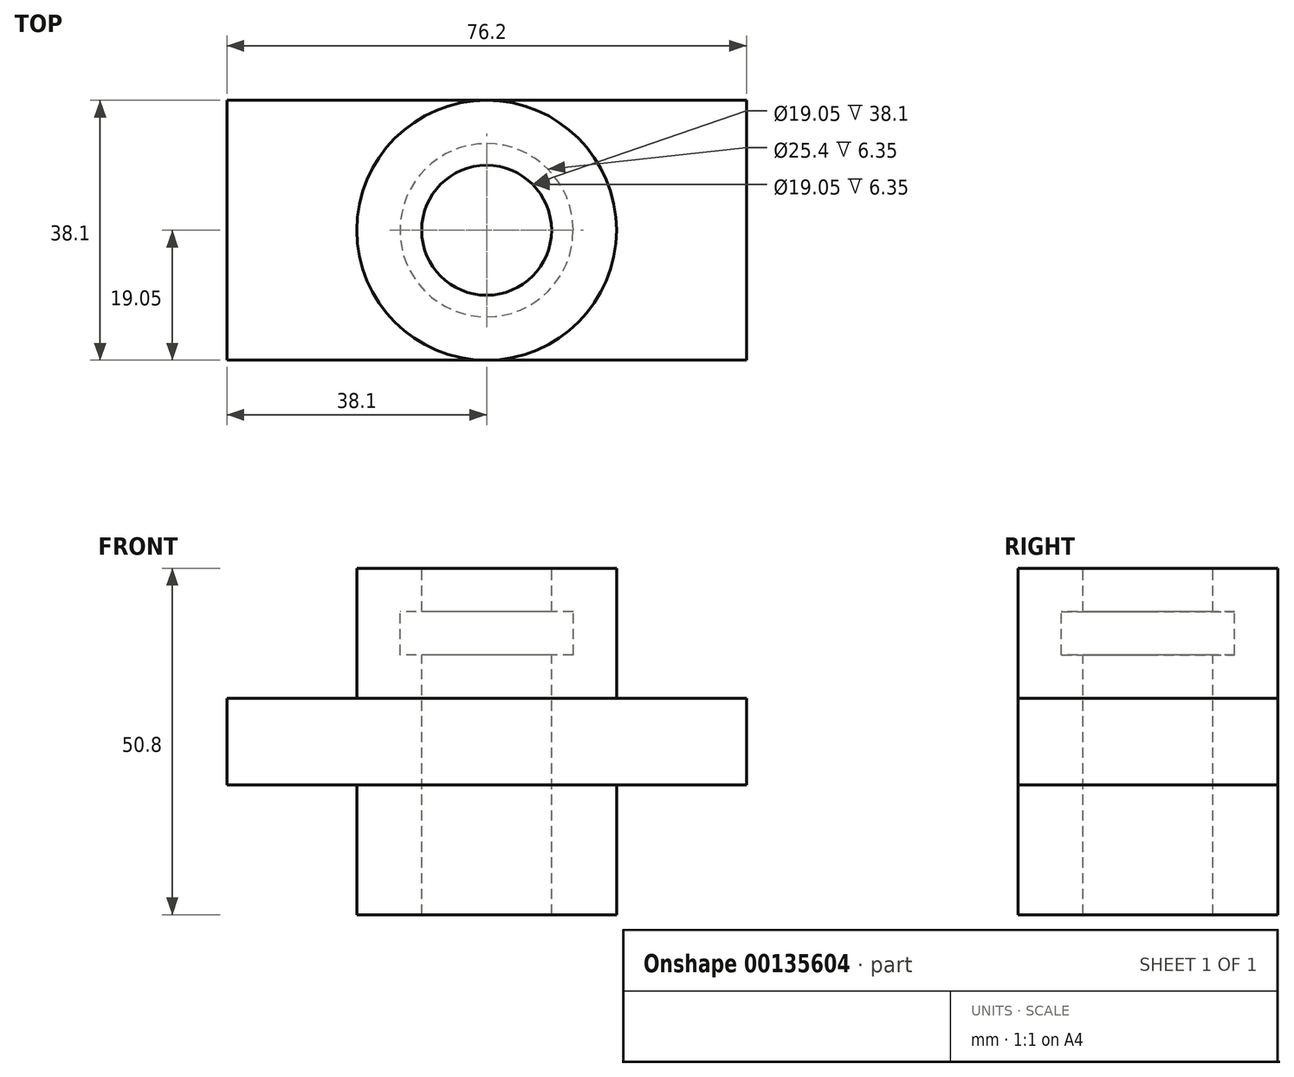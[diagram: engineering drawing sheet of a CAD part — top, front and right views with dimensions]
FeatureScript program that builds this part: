
annotation { "Feature Type Name" : "Feature", "Feature Type Description" : "" }
export const myFeature = defineFeature(function(context is Context, id is Id, definition is map)
    precondition{}
    {
        {
            var Q0;
            Q0=qCreatedBy(makeId("Front.planeOp"),FACE);
            var sketch = newSketch(context, id + "F0", { "sketchPlane" : qUnion([Q0])});
            skLineSegment(sketch, "E0", {"start": v(0, -46.63) * mm, "end": v(0, 59.55) * mm, "construction": true});
            skLineSegment(sketch, "E1", {"start": v(0, 50.8) * mm, "end": v(19.05, 50.8) * mm});
            skLineSegment(sketch, "E2", {"start": v(19.05, 50.8) * mm, "end": v(19.05, 31.75) * mm});
            skLineSegment(sketch, "E3", {"start": v(19.05, 31.75) * mm, "end": v(0, 31.75) * mm});
            skLineSegment(sketch, "E4", {"start": v(19.05, 31.75) * mm, "end": v(38.1, 31.75) * mm});
            skLineSegment(sketch, "E5", {"start": v(38.1, 31.75) * mm, "end": v(38.1, 19.05) * mm});
            skLineSegment(sketch, "E6", {"start": v(38.1, 19.05) * mm, "end": v(0, 19.05) * mm});
            skLineSegment(sketch, "E7", {"start": v(19.05, 19.05) * mm, "end": v(19.05, 0) * mm});
            skLineSegment(sketch, "E8", {"start": v(19.05, 0) * mm, "end": v(0, 0) * mm});
            skLineSegment(sketch, "E9", {"start": v(9.52, 50.8) * mm, "end": v(9.52, 44.45) * mm});
            skLineSegment(sketch, "E10", {"start": v(12.7, 44.45) * mm, "end": v(0, 44.45) * mm});
            skLineSegment(sketch, "E11", {"start": v(12.7, 44.45) * mm, "end": v(12.7, 38.1) * mm});
            skLineSegment(sketch, "E12", {"start": v(12.7, 38.1) * mm, "end": v(0, 38.1) * mm});
            skLineSegment(sketch, "E13", {"start": v(9.52, 38.1) * mm, "end": v(9.53, 0) * mm});
            skLineSegment(sketch, "E14", {"start": v(0, 0) * mm, "end": v(0, 50.8) * mm});
            skSolve(sketch);
        }
        {
            var Q0;
            Q0 = qSketchRegion(id + "F0", true);
            var Q1;
            Q1=sQuery(id+"F0.wireOp",EDGE,"E14");
            revolve(context, id + "F1", {"entities" : qUnion([Q0]), "axis" : qUnion([Q1]), "revolveType" : RevolveType.FULL});
        }
        {
            var Q0;
            Q0=makeQuery(id+"F1.opRevolve","SWEPT_FACE",FACE,{"disambiguationData":[OSD([sQuery(id+"F0.wireOp",EDGE,"E4")])]});
            var sketch = newSketch(context, id + "F2", { "sketchPlane" : qUnion([Q0])});
            skLineSegment(sketch, "E15.bottom", {"start": v(-38.1, 19.05) * mm, "end": v(38.1, 19.05) * mm});
            skLineSegment(sketch, "E15.top", {"start": v(-38.1, -19.05) * mm, "end": v(38.1, -19.05) * mm});
            skLineSegment(sketch, "E15.left", {"start": v(-38.1, 19.05) * mm, "end": v(-38.1, -19.05) * mm});
            skLineSegment(sketch, "E15.right", {"start": v(38.1, 19.05) * mm, "end": v(38.1, -19.05) * mm});
            skLineSegment(sketch, "E16", {"start": v(0, -49.24) * mm, "end": v(0, 75.23) * mm, "construction": true});
            skLineSegment(sketch, "E17", {"start": v(-65, 0) * mm, "end": v(64.27, 0) * mm, "construction": true});
            skSolve(sketch);
        }
        {
            var Q0;
            {var subQ0=sQuery(id+"F2.wireOp",EDGE,"E15.bottom");var subQ1=sQuery(id+"F0.wireOp",EDGE,"E4");var subQ2=makeQuery(id+"F1.opRevolve","SWEPT_EDGE",EDGE,{"disambiguationData":[OSD([subQ1,sQuery(id+"F0.wireOp",EDGE,"E5")])]});var subQ3=makeQuery(id+"F2.imprint","INTERSECT",VERTEX,{"disambiguationData":[OD(0.0)],"derivedFrom":[subQ2,subQ0]});Q0=makeQuery(id+"F2.imprint","IMPRINT",FACE,{"disambiguationData":[TD([[makeQuery(id+"F2.imprint","IMPRINT",EDGE,{"disambiguationData":[TD([[subQ3,-1.0]])],"derivedFrom":subQ0}),1.0]])]});}
            var Q1;
            {var subQ0=sQuery(id+"F2.wireOp",EDGE,"E15.top");var subQ1=sQuery(id+"F0.wireOp",EDGE,"E4");var subQ2=makeQuery(id+"F1.opRevolve","SWEPT_EDGE",EDGE,{"disambiguationData":[OSD([subQ1,sQuery(id+"F0.wireOp",EDGE,"E5")])]});var subQ3=makeQuery(id+"F2.imprint","INTERSECT",VERTEX,{"disambiguationData":[OD(0.0)],"derivedFrom":[subQ2,subQ0]});Q1=makeQuery(id+"F2.imprint","IMPRINT",FACE,{"disambiguationData":[TD([[makeQuery(id+"F2.imprint","IMPRINT",EDGE,{"disambiguationData":[TD([[subQ3,-1.0]])],"derivedFrom":subQ0}),-1.0]])]});}
            extrude(context, id + "F3", {"entities" : qUnion([Q0, Q1]), "operationType" : NewBodyOperationType.REMOVE, "endBound" : BoundingType.THROUGH_ALL, "oppositeDirection" : true, "depth" : 25.4 * mm});
        }
        {
            var Q0;
            {var subQ0=sQuery(id+"F2.wireOp",EDGE,"E15.top");var subQ1=sQuery(id+"F0.wireOp",EDGE,"E4");var subQ2=makeQuery(id+"F1.opRevolve","SWEPT_EDGE",EDGE,{"disambiguationData":[OSD([subQ1,sQuery(id+"F0.wireOp",EDGE,"E5")])]});var subQ3=makeQuery(id+"F2.imprint","INTERSECT",VERTEX,{"disambiguationData":[OD(0.0)],"derivedFrom":[subQ2,subQ0]});Q0=makeQuery(id+"F2.imprint","IMPRINT",FACE,{"disambiguationData":[TD([[makeQuery(id+"F2.imprint","IMPRINT",EDGE,{"disambiguationData":[TD([[subQ3,-1.0]])],"derivedFrom":subQ0}),-1.0]])]});}
            var sketch = newSketch(context, id + "F4", { "sketchPlane" : qUnion([Q0])});
            skLineSegment(sketch, "E18.0.0", {"start": v(-33, 19.05) * mm, "end": v(-38.1, 19.05) * mm});
            skLineSegment(sketch, "E18.0.1", {"start": v(-38.1, 19.05) * mm, "end": v(-38.1, 0) * mm});
            skArc(sketch, "E18.0.2", {"start": v(-38.1, 0) * mm, "mid": v(-36.8, 9.86) * mm, "end": v(-33, 19.05) * mm});
            skLineSegment(sketch, "E19.0.0", {"start": v(-38.1, 0) * mm, "end": v(-38.1, -19.05) * mm});
            skLineSegment(sketch, "E19.0.1", {"start": v(-38.1, -19.05) * mm, "end": v(-33, -19.05) * mm});
            skArc(sketch, "E19.0.2", {"start": v(-33, -19.05) * mm, "mid": v(-36.8, -9.86) * mm, "end": v(-38.1, 0) * mm});
            skLineSegment(sketch, "E20.0.0", {"start": v(38.1, 19.05) * mm, "end": v(33, 19.05) * mm});
            skArc(sketch, "E20.0.1", {"start": v(33, 19.05) * mm, "mid": v(36.8, 9.86) * mm, "end": v(38.1, 0) * mm});
            skLineSegment(sketch, "E20.0.2", {"start": v(38.1, 0) * mm, "end": v(38.1, 19.05) * mm});
            skArc(sketch, "E21.0.0", {"start": v(38.1, 0) * mm, "mid": v(36.8, -9.86) * mm, "end": v(33, -19.05) * mm});
            skLineSegment(sketch, "E21.0.1", {"start": v(33, -19.05) * mm, "end": v(38.1, -19.05) * mm});
            skLineSegment(sketch, "E21.0.2", {"start": v(38.1, -19.05) * mm, "end": v(38.1, 0) * mm});
            skSolve(sketch);
        }
        {
            var Q0;
            Q0 = qSketchRegion(id + "F4", true);
            var Q1;
            Q1=makeQuery(id+"F3.boolean.opBoolean","SPLIT",FACE,{"disambiguationData":[OD(1.0)],"derivedFrom":makeQuery(id+"F1.opRevolve","SWEPT_FACE",FACE,{"disambiguationData":[OSD([sQuery(id+"F0.wireOp",EDGE,"E6")])]})});
            extrude(context, id + "F5", {"entities" : qUnion([Q0]), "operationType" : NewBodyOperationType.ADD, "endBound" : BoundingType.UP_TO_SURFACE, "oppositeDirection" : true, "endBoundEntityFace" : qUnion([Q1]), "depth" : 25.4 * mm});
        }
        {
            var Q0;
            Q0=qCreatedBy(makeId("Front.planeOp"),FACE);
            var sketch = newSketch(context, id + "F6", { "sketchPlane" : qUnion([Q0])});
            skLineSegment(sketch, "E22", {"start": v(0, -8.47) * mm, "end": v(0, 69.33) * mm, "construction": true});
            skLineSegment(sketch, "E23", {"start": v(0, 50.8) * mm, "end": v(9.52, 50.8) * mm});
            skLineSegment(sketch, "E24", {"start": v(9.52, 50.8) * mm, "end": v(9.52, 44.45) * mm});
            skLineSegment(sketch, "E25", {"start": v(0, 44.45) * mm, "end": v(12.7, 44.45) * mm});
            skLineSegment(sketch, "E26", {"start": v(12.7, 44.45) * mm, "end": v(12.7, 38.1) * mm});
            skLineSegment(sketch, "E27", {"start": v(12.7, 38.1) * mm, "end": v(0, 38.1) * mm});
            skLineSegment(sketch, "E28", {"start": v(9.52, 38.1) * mm, "end": v(9.52, 0) * mm});
            skLineSegment(sketch, "E29", {"start": v(9.52, 0) * mm, "end": v(0, 0) * mm});
            skLineSegment(sketch, "E30", {"start": v(0, 0) * mm, "end": v(0, 50.8) * mm});
            skSolve(sketch);
        }
        {
            var Q0;
            Q0 = qSketchRegion(id + "F6", true);
            var Q1;
            Q1=sQuery(id+"F6.wireOp",EDGE,"E22");
            revolve(context, id + "F7", {"operationType" : NewBodyOperationType.REMOVE, "entities" : qUnion([Q0]), "axis" : qUnion([Q1]), "revolveType" : RevolveType.FULL, "oppositeDirection" : true});
        }
    });
